# Revit family: Basin-Wall-Caroma Cubus Utility1
name_source: partatom
category: Plumbing Fixtures
revit_build: Autodesk Revit Architecture 2012 (Build: 20110916_2132(x64)
units: mm (PartAtom-declared; Revit-internal decimal feet)

## types (1)
- 1 Tap Hole
    1 Taphole = Yes
    Assembly Code = D2010310
    BowlCapacity_ANZRS = 0.01 m³
    CW Connection = No
    Cost = 419 $
    Default Elevation = 865 mm  [stored 2.83793 ft]
    Description = Caroma Cubus Utility Wall Basin
    HW Connection = No
    Height_ANZRS = 214 mm  [stored 0.7021 ft]
    Keynote = UB
    Length_ANZRS = 550 mm
    Manufacturer = Caroma
    Material_ANZRS = Porcelain-White-Caroma
    Model = 633615W
    PlumbingMaterial_ANZRS = PVC-White-Caroma
    Spout Penetration = 0 mm  [stored 0 ft]
    Type Comments = Ceramic Wall Basin supplied 40mm trap connection.  Alternative waste options available. 13 litres to overflow.  White only
    URL = http://www.caroma.com.au
    Vent Connection = No
    WFU = 3
    Waste = Metal-Chrome-Caroma
    Waste Connection = Yes
    Width_ANZRS = 400 mm  [stored 1.31234 ft]

note: [stored X ft] marks values corroborated as IEEE doubles in the binary element streams (Revit-internal decimal feet)

## geometry (parser evidence)
native form markers: Blend x4, Sweep x1
no freeform markers — native parametric forms only
